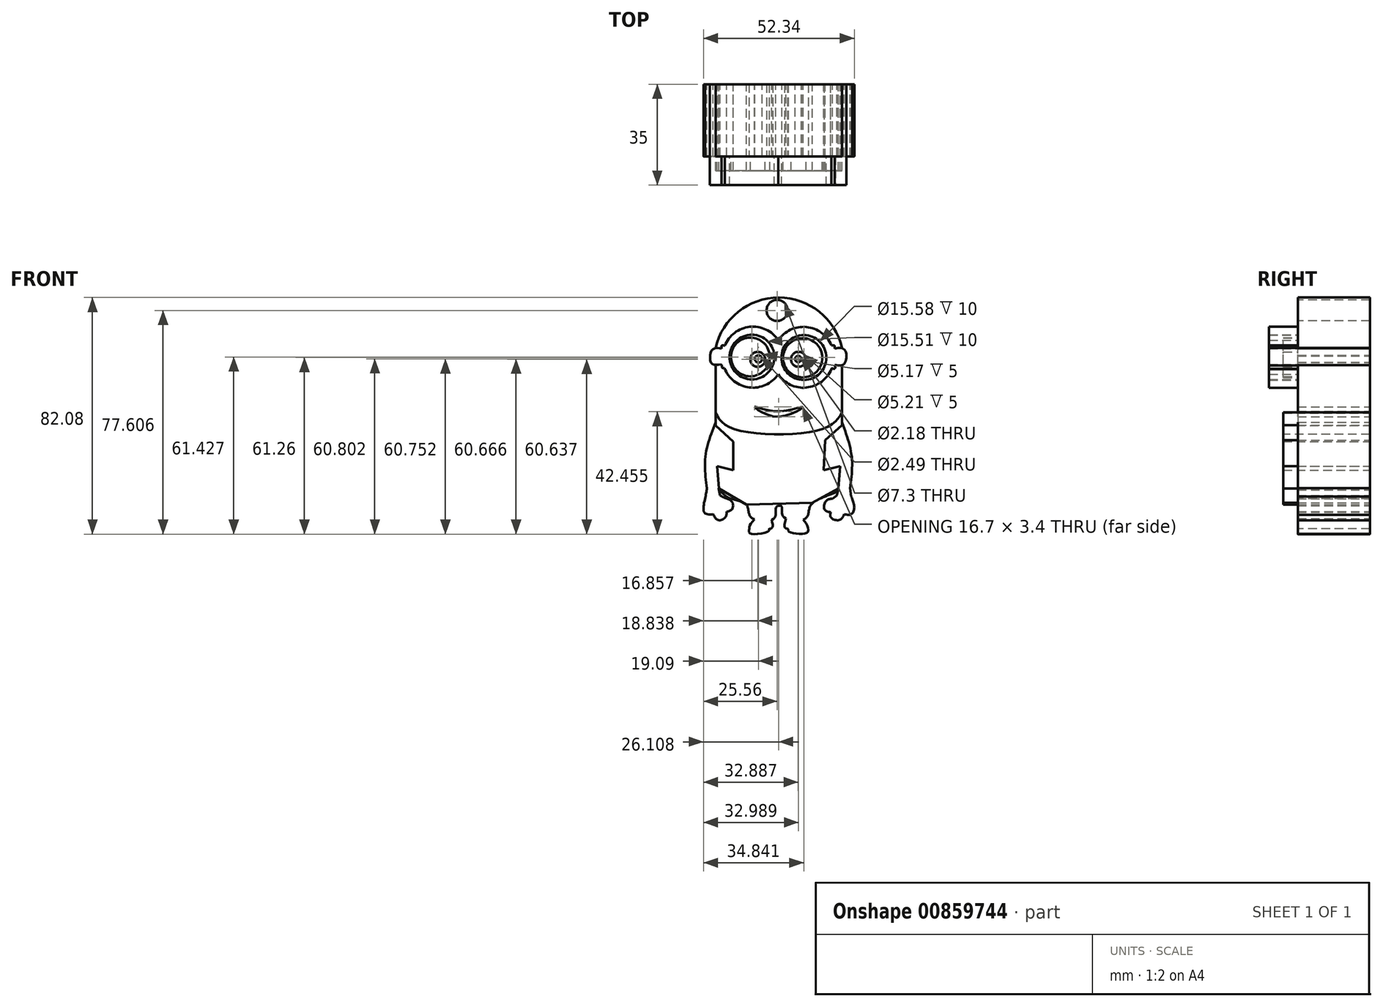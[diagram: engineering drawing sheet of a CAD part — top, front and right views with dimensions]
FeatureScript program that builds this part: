
annotation { "Feature Type Name" : "Feature", "Feature Type Description" : "" }
export const myFeature = defineFeature(function(context is Context, id is Id, definition is map)
    precondition{}
    {
        {
            var Q0;
            Q0=qCreatedBy(makeId("Front.planeOp"),FACE);
            var sketch = newSketch(context, id + "F0", { "sketchPlane" : qUnion([Q0])});
            skCircle(sketch, "E0", {"center": v(9.28, 20.5) * mm, "radius": 7.79 * mm});
            skPoint(sketch, "E0.first.point", {"position": v(9.52, 28.28) * mm});
            skPoint(sketch, "E0.second.point", {"position": v(17.06, 20.1) * mm});
            skPoint(sketch, "E0.third.point", {"position": v(3.92, 14.85) * mm});
            skCircle(sketch, "E1", {"center": v(-8.7, 20.67) * mm, "radius": 7.75 * mm});
            skPoint(sketch, "E1.first.point", {"position": v(-9.22, 28.4) * mm});
            skPoint(sketch, "E1.second.point", {"position": v(-0.97, 20.1) * mm});
            skPoint(sketch, "E1.third.point", {"position": v(-16.11, 18.39) * mm});
            skArc(sketch, "E2", {"start": v(0.4, 26.53) * mm, "mid": v(-18.96, 20.65) * mm, "end": v(0.38, 14.7) * mm});
            skPoint(sketch, "E2.first.point", {"position": v(-8.74, 31.2) * mm});
            skPoint(sketch, "E2.second.point", {"position": v(-8.44, 10.05) * mm});
            skPoint(sketch, "E2.third.point", {"position": v(-18.93, 19.83) * mm});
            skArc(sketch, "E3", {"start": v(0.38, 14.7) * mm, "mid": v(19.7, 20.59) * mm, "end": v(0.4, 26.53) * mm});
            skPoint(sketch, "E3.first.point", {"position": v(9.59, 31.15) * mm});
            skPoint(sketch, "E3.second.point", {"position": v(19.66, 19.83) * mm});
            skPoint(sketch, "E3.third.point", {"position": v(8, 10.11) * mm});
            skFitSpline(sketch, "E4", {"points": [v(18.85, 24.73) * mm, v(19.87, 24.63) * mm, v(19.97, 23.65) * mm], "startDerivative": vector(2.5, 0.28) * mm, "endDerivative": vector(-0.27, -2.43) * mm});
            skFitSpline(sketch, "E5", {"points": [v(19.97, 23.65) * mm, v(23.52, 23.1) * mm, v(23.29, 18.32) * mm, v(20.01, 18) * mm], "startDerivative": vector(13.3, 1.85) * mm, "endDerivative": vector(-12.33, 2.55) * mm});
            skFitSpline(sketch, "E6", {"points": [v(20.01, 18) * mm, v(20.01, 16.69) * mm, v(18.94, 16.7) * mm, v(18.85, 16.48) * mm], "startDerivative": vector(1, -4.05) * mm, "endDerivative": vector(-0.02, -1.55) * mm});
            skFitSpline(sketch, "E7", {"points": [v(-18.17, 24.63) * mm, v(-19.18, 24.63) * mm, v(-19.25, 23.65) * mm], "startDerivative": vector(-2.46, 0.5) * mm, "endDerivative": vector(0.31, -2.46) * mm});
            skFitSpline(sketch, "E8", {"points": [v(-19.25, 23.65) * mm, v(-22.57, 23.1) * mm, v(-22.44, 18.29) * mm, v(-19.25, 18) * mm, v(-19.07, 17.04) * mm, v(-18.29, 16.92) * mm], "startDerivative": vector(-16.18, 2.6) * mm, "endDerivative": vector(8.86, 1.17) * mm});
            skCircle(sketch, "E9", {"center": v(-9.3, 20.73) * mm, "radius": 6.74 * mm});
            skPoint(sketch, "E9.first.point", {"position": v(-8.05, 27.35) * mm});
            skPoint(sketch, "E9.second.point", {"position": v(-9.11, 14) * mm});
            skPoint(sketch, "E9.third.point", {"position": v(-10.63, 14.13) * mm});
            skCircle(sketch, "E10", {"center": v(-6.72, 19.88) * mm, "radius": 2.58 * mm});
            skPoint(sketch, "E10.first.point", {"position": v(-6.73, 22.46) * mm});
            skPoint(sketch, "E10.second.point", {"position": v(-6.53, 17.3) * mm});
            skPoint(sketch, "E10.third.point", {"position": v(-8.98, 18.62) * mm});
            skCircle(sketch, "E11", {"center": v(-6.47, 20.04) * mm, "radius": 1.25 * mm});
            skPoint(sketch, "E11.first.point", {"position": v(-7.06, 21.14) * mm});
            skPoint(sketch, "E11.second.point", {"position": v(-6.72, 18.82) * mm});
            skPoint(sketch, "E11.third.point", {"position": v(-7.46, 19.29) * mm});
            skCircle(sketch, "E12", {"center": v(7.33, 20) * mm, "radius": 1.1 * mm});
            skPoint(sketch, "E12.first.point", {"position": v(7.16, 21.07) * mm});
            skPoint(sketch, "E12.second.point", {"position": v(8.41, 19.88) * mm});
            skPoint(sketch, "E12.third.point", {"position": v(6.5, 19.29) * mm});
            skCircle(sketch, "E13", {"center": v(7.43, 19.9) * mm, "radius": 2.6 * mm});
            skPoint(sketch, "E13.first.point", {"position": v(8.55, 22.26) * mm});
            skPoint(sketch, "E13.second.point", {"position": v(7.33, 17.3) * mm});
            skPoint(sketch, "E13.third.point", {"position": v(5.24, 18.5) * mm});
            skCircle(sketch, "E14", {"center": v(8.89, 20.42) * mm, "radius": 6.8 * mm});
            skPoint(sketch, "E14.first.point", {"position": v(10.53, 27.02) * mm});
            skPoint(sketch, "E14.second.point", {"position": v(11.46, 14.13) * mm});
            skPoint(sketch, "E14.third.point", {"position": v(3.92, 15.78) * mm});
            skSolve(sketch);
        }
        {
            var Q0;
            Q0=qCreatedBy(makeId("Front.planeOp"),FACE);
            var sketch = newSketch(context, id + "F1", { "sketchPlane" : qUnion([Q0])});
            skArc(sketch, "E15", {"start": v(22.5, 23.85) * mm, "mid": v(0.59, 41.32) * mm, "end": v(-21.33, 23.85) * mm});
            skPoint(sketch, "E15.first.point", {"position": v(0, 41.3) * mm});
            skPoint(sketch, "E15.second.point", {"position": v(22.5, 23.85) * mm});
            skPoint(sketch, "E15.third.point", {"position": v(-21.33, 23.85) * mm});
            skLineSegment(sketch, "E16.left", {"start": v(22.5, 23.85) * mm, "end": v(22.5, -1.97) * mm});
            skLineSegment(sketch, "E16.right", {"start": v(-21.33, 23.85) * mm, "end": v(-21.33, -1.97) * mm});
            skFitSpline(sketch, "E17", {"points": [v(-21.33, -1.97) * mm, v(-24.85, -13.62) * mm, v(-24.35, -24.85) * mm], "startDerivative": vector(-8.93, -22.82) * mm, "endDerivative": vector(2.96, -22.94) * mm});
            skFitSpline(sketch, "E18", {"points": [v(-19.42, -9.62) * mm, v(-21.04, -17.3) * mm, v(-20.3, -24.79) * mm], "startDerivative": vector(-4.4, -15.21) * mm, "endDerivative": vector(2.68, -15.12) * mm});
            skFitSpline(sketch, "E19", {"points": [v(22.5, -1.97) * mm, v(25.85, -13.64) * mm, v(25.32, -24.79) * mm], "startDerivative": vector(8.52, -22.88) * mm, "endDerivative": vector(-2.95, -22.75) * mm});
            skFitSpline(sketch, "E20", {"points": [v(20.43, -9.8) * mm, v(21.95, -15.7) * mm, v(21.35, -24.79) * mm], "startDerivative": vector(4.39, -12.32) * mm, "endDerivative": vector(-2.31, -17.47) * mm});
            skFitSpline(sketch, "E21", {"points": [v(-24.35, -24.85) * mm, v(-24.89, -27.96) * mm, v(-25.28, -33.24) * mm, v(-22.16, -33.85) * mm], "startDerivative": vector(-1.2, -8.73) * mm, "endDerivative": vector(12.85, 0.91) * mm});
            skFitSpline(sketch, "E22", {"points": [v(-22.16, -33.85) * mm, v(-20.3, -35.9) * mm, v(-17.88, -34.8) * mm, v(-17.55, -32.96) * mm], "startDerivative": vector(4.35, -7.95) * mm, "endDerivative": vector(-0.37, 6.48) * mm});
            skFitSpline(sketch, "E23", {"points": [v(-17.55, -32.96) * mm, v(-15.71, -32.18) * mm, v(-15.32, -30.24) * mm, v(-16.32, -28.85) * mm, v(-17.55, -28.4) * mm, v(-19.77, -27.29) * mm], "startDerivative": vector(10.29, 2.19) * mm, "endDerivative": vector(-10.31, 5.77) * mm});
            skFitSpline(sketch, "E24", {"points": [v(-19.77, -27.29) * mm, v(-20.3, -24.79) * mm], "startDerivative": vector(-0.52, 2.5) * mm, "endDerivative": vector(-0.52, 2.5) * mm});
            skFitSpline(sketch, "E25", {"points": [v(25.32, -24.79) * mm, v(25.72, -27.73) * mm], "startDerivative": vector(0.4, -2.94) * mm, "endDerivative": vector(0.4, -2.94) * mm});
            skFitSpline(sketch, "E26", {"points": [v(25.72, -27.73) * mm, v(26.66, -30.4) * mm, v(26.55, -32.74) * mm, v(25.32, -33.96) * mm, v(23.33, -33.8) * mm], "startDerivative": vector(4.04, -9.36) * mm, "endDerivative": vector(-8.88, 2.18) * mm});
            skFitSpline(sketch, "E27", {"points": [v(23.33, -33.8) * mm, v(22.1, -35.57) * mm, v(19.99, -35.8) * mm, v(18.49, -34.57) * mm, v(18.6, -33.13) * mm], "startDerivative": vector(-3.66, -7.88) * mm, "endDerivative": vector(1.93, 6.8) * mm});
            skFitSpline(sketch, "E28", {"points": [v(18.6, -33.13) * mm, v(16.65, -32.4) * mm, v(16.37, -30.4) * mm, v(17.65, -28.73) * mm, v(19.21, -28.51) * mm], "startDerivative": vector(-8.86, 1.43) * mm, "endDerivative": vector(7.12, -0.19) * mm});
            skFitSpline(sketch, "E29", {"points": [v(19.21, -28.51) * mm, v(20.71, -27.29) * mm], "startDerivative": vector(1.5, 1.22) * mm, "endDerivative": vector(1.5, 1.22) * mm});
            skFitSpline(sketch, "E30", {"points": [v(20.71, -27.29) * mm, v(21.35, -24.79) * mm], "startDerivative": vector(0.64, 2.5) * mm, "endDerivative": vector(0.64, 2.5) * mm});
            skFitSpline(sketch, "E31", {"points": [v(-20.3, -24.79) * mm, v(-16.53, -28.27) * mm, v(-10.59, -30.63) * mm, v(-8.93, -35) * mm, v(-0.9, -35.12) * mm, v(-0.32, -31.43) * mm, v(1.52, -31.1) * mm, v(2.18, -34.7) * mm, v(9.99, -35.22) * mm, v(11.81, -30.54) * mm, v(20.71, -25.96) * mm, v(21.35, -24.79) * mm], "startDerivative": vector(32.18, -43.66) * mm, "endDerivative": vector(2.2, 24.18) * mm});
            skFitSpline(sketch, "E32", {"points": [v(-1.9, -35.78) * mm, v(-1.55, -37.96) * mm, v(-2.14, -38.83) * mm, v(-2.76, -38.88) * mm, v(-2.84, -39.52) * mm, v(-7.07, -40.74) * mm, v(-9.67, -40.24) * mm, v(-9.67, -39.15) * mm, v(-9.55, -37.96) * mm, v(-7.9, -35.62) * mm], "startDerivative": vector(5.3, -18.32) * mm, "endDerivative": vector(14.78, 17.3) * mm});
            skFitSpline(sketch, "E33", {"points": [v(9.07, -35.7) * mm, v(10.5, -37.81) * mm, v(10.76, -39.87) * mm, v(9.2, -40.64) * mm, v(5.31, -40.34) * mm, v(3.83, -39.55) * mm, v(3.78, -38.93) * mm, v(3.16, -38.78) * mm, v(2.56, -38.23) * mm, v(3.05, -35.39) * mm], "startDerivative": vector(11.76, -14.6) * mm, "endDerivative": vector(6.8, 23.47) * mm});
            skFitSpline(sketch, "E34", {"points": [v(-7.8, 3.4) * mm, v(0, 1.83) * mm, v(8.9, 3.32) * mm, v(0, 0) * mm, v(-7.8, 3.4) * mm]});
            skLineSegment(sketch, "E35", {"start": v(25.32, -24.79) * mm, "end": v(21.35, -24.79) * mm});
            skLineSegment(sketch, "E36", {"start": v(-20.3, -24.79) * mm, "end": v(-24.35, -24.85) * mm});
            skSolve(sketch);
        }
        {
            var Q0;
            Q0=qCreatedBy(makeId("Front.planeOp"),FACE);
            var sketch = newSketch(context, id + "F2", { "sketchPlane" : qUnion([Q0])});
            skFitSpline(sketch, "E37", {"points": [v(-21.36, 1.21) * mm, v(-15.26, -4.16) * mm, v(16.06, -4.18) * mm, v(22.5, 1.46) * mm], "startDerivative": vector(14.47, -24.14) * mm, "endDerivative": vector(15.11, 24.76) * mm});
            skFitSpline(sketch, "E38", {"points": [v(22.5, 1.46) * mm, v(22.5, -2.9) * mm], "startDerivative": vector(0, -4.36) * mm, "endDerivative": vector(0, -4.36) * mm});
            skFitSpline(sketch, "E39", {"points": [v(22.5, -2.9) * mm, v(16.6, -8.2) * mm], "startDerivative": vector(-5.9, -5.3) * mm, "endDerivative": vector(-5.9, -5.3) * mm});
            skFitSpline(sketch, "E40", {"points": [v(16.6, -8.2) * mm, v(16.11, -18.6) * mm], "startDerivative": vector(-0.5, -10.4) * mm, "endDerivative": vector(-0.5, -10.4) * mm});
            skFitSpline(sketch, "E41", {"points": [v(16.11, -18.6) * mm, v(21.86, -17.18) * mm], "startDerivative": vector(5.75, 1.42) * mm, "endDerivative": vector(5.75, 1.42) * mm});
            skFitSpline(sketch, "E42", {"points": [v(21.86, -17.18) * mm, v(21.2, -24.9) * mm], "startDerivative": vector(-0.65, -7.72) * mm, "endDerivative": vector(-0.65, -7.72) * mm});
            skFitSpline(sketch, "E43", {"points": [v(21.2, -24.9) * mm, v(12.17, -29.91) * mm], "startDerivative": vector(-9.03, -5.01) * mm, "endDerivative": vector(-9.03, -5.01) * mm});
            skFitSpline(sketch, "E44", {"points": [v(12.17, -29.91) * mm, v(-10.66, -30.54) * mm], "startDerivative": vector(-22.83, -0.63) * mm, "endDerivative": vector(-22.83, -0.63) * mm});
            skFitSpline(sketch, "E45", {"points": [v(-10.66, -30.54) * mm, v(-20.1, -24.9) * mm], "startDerivative": vector(-9.45, 5.64) * mm, "endDerivative": vector(-9.45, 5.64) * mm});
            skFitSpline(sketch, "E46", {"points": [v(-20.1, -24.9) * mm, v(-20.83, -17.18) * mm], "startDerivative": vector(-0.72, 7.72) * mm, "endDerivative": vector(-0.72, 7.72) * mm});
            skFitSpline(sketch, "E47", {"points": [v(-20.83, -17.18) * mm, v(-15.27, -18.6) * mm], "startDerivative": vector(5.56, -1.42) * mm, "endDerivative": vector(5.56, -1.42) * mm});
            skFitSpline(sketch, "E48", {"points": [v(-15.27, -18.6) * mm, v(-15.27, -8.65) * mm], "startDerivative": vector(0, 9.95) * mm, "endDerivative": vector(0, 9.95) * mm});
            skFitSpline(sketch, "E49", {"points": [v(-15.27, -8.65) * mm, v(-21.28, -3.05) * mm], "startDerivative": vector(-6, 5.6) * mm, "endDerivative": vector(-6, 5.6) * mm});
            skFitSpline(sketch, "E50", {"points": [v(-21.28, -3.05) * mm, v(-21.36, 1.21) * mm], "startDerivative": vector(-0.08, 4.26) * mm, "endDerivative": vector(-0.08, 4.26) * mm});
            skSolve(sketch);
        }
        {
            var Q0;
            Q0 = qSketchRegion(id + "F1", true);
            extrude(context, id + "F3", {"entities" : qUnion([Q0]), "depth" : 25 * mm, "offsetDistance" : 25 * mm});
        }
        {
            var Q0;
            Q0=makeQuery(id+"F0.imprint","IMPRINT",FACE,{"disambiguationData":[TD([[makeQuery(id+"F0.imprint","IMPRINT",EDGE,{"derivedFrom":sQuery(id+"F0.wireOp",EDGE,"E0")}),-1.0]])]});
            var Q1;
            {var subQ0=sQuery(id+"F0.wireOp",EDGE,"E4");Q1=makeQuery(id+"F0.imprint","IMPRINT",FACE,{"disambiguationData":[TD([[makeQuery(id+"F0.imprint","IMPRINT",EDGE,{"derivedFrom":subQ0}),-1.0]])]});}
            var Q2;
            {var subQ0=sQuery(id+"F0.wireOp",EDGE,"E7");Q2=makeQuery(id+"F0.imprint","IMPRINT",FACE,{"disambiguationData":[TD([[makeQuery(id+"F0.imprint","IMPRINT",EDGE,{"derivedFrom":subQ0}),1.0]])]});}
            extrude(context, id + "F4", {"entities" : qUnion([Q0, Q1, Q2]), "operationType" : NewBodyOperationType.ADD, "depth" : 35 * mm, "offsetDistance" : 25 * mm});
        }
        {
            var Q0;
            Q0=makeQuery(id+"F0.imprint","IMPRINT",FACE,{"disambiguationData":[TD([[makeQuery(id+"F0.imprint","IMPRINT",EDGE,{"derivedFrom":sQuery(id+"F0.wireOp",EDGE,"E13")}),-1.0]])]});
            var Q1;
            Q1=makeQuery(id+"F0.imprint","IMPRINT",FACE,{"disambiguationData":[TD([[makeQuery(id+"F0.imprint","IMPRINT",EDGE,{"derivedFrom":sQuery(id+"F0.wireOp",EDGE,"E9")}),1.0]])]});
            extrude(context, id + "F5", {"entities" : qUnion([Q0, Q1]), "operationType" : NewBodyOperationType.ADD, "depth" : 30 * mm, "offsetDistance" : 25 * mm});
        }
        {
            var Q0;
            Q0=makeQuery(id+"F0.imprint","IMPRINT",FACE,{"disambiguationData":[TD([[makeQuery(id+"F0.imprint","IMPRINT",EDGE,{"derivedFrom":sQuery(id+"F0.wireOp",EDGE,"E12")}),1.0]])]});
            var Q1;
            Q1=makeQuery(id+"F0.imprint","IMPRINT",FACE,{"disambiguationData":[TD([[makeQuery(id+"F0.imprint","IMPRINT",EDGE,{"derivedFrom":sQuery(id+"F0.wireOp",EDGE,"E11")}),1.0]])]});
            extrude(context, id + "F6", {"entities" : qUnion([Q0, Q1]), "operationType" : NewBodyOperationType.REMOVE, "endBound" : BoundingType.THROUGH_ALL, "depth" : 42.6 * mm, "offsetDistance" : 25 * mm});
        }
        {
            var Q0;
            Q0=makeQuery(id+"F2.imprint","IMPRINT",FACE,{"disambiguationData":[TD([[makeQuery(id+"F2.imprint","IMPRINT",EDGE,{"derivedFrom":sQuery(id+"F2.wireOp",EDGE,"E37")}),-1.0]])]});
            extrude(context, id + "F7", {"entities" : qUnion([Q0]), "depth" : 30 * mm, "offsetDistance" : 25 * mm});
        }
        {
            var Q0;
            {var subQ0=sQuery(id+"F1.wireOp",EDGE,"E16.right");var subQ2=sQuery(id+"F1.wireOp",EDGE,"E16.left");var subQ6=sQuery(id+"F1.wireOp",EDGE,"E15");Q0=makeQuery(id+"F4.boolean.opBoolean","SPLIT",FACE,{"disambiguationData":[TD([makeQuery(id+"F3.opExtrude","SWEPT_FACE",FACE,{"disambiguationData":[OSD([subQ6])]})])],"derivedFrom":makeQuery(id+"F3.opExtrude","CAP_FACE",FACE,{"disambiguationData":[OSD([subQ6,subQ2,subQ0,sQuery(id+"F1.wireOp",EDGE,"E17"),sQuery(id+"F1.wireOp",EDGE,"E19"),sQuery(id+"F1.wireOp",EDGE,"E21"),sQuery(id+"F1.wireOp",EDGE,"E22"),sQuery(id+"F1.wireOp",EDGE,"E23"),sQuery(id+"F1.wireOp",EDGE,"E24"),sQuery(id+"F1.wireOp",EDGE,"E25"),sQuery(id+"F1.wireOp",EDGE,"E26"),sQuery(id+"F1.wireOp",EDGE,"E27"),sQuery(id+"F1.wireOp",EDGE,"E28"),sQuery(id+"F1.wireOp",EDGE,"E29"),sQuery(id+"F1.wireOp",EDGE,"E30"),sQuery(id+"F1.wireOp",EDGE,"E31"),sQuery(id+"F1.wireOp",EDGE,"E32"),sQuery(id+"F1.wireOp",EDGE,"E33"),sQuery(id+"F1.wireOp",EDGE,"E34")])],"isStart":false})});}
            var sketch = newSketch(context, id + "F8", { "sketchPlane" : qUnion([Q0])});
            skCircle(sketch, "E51", {"center": v(0, 36.85) * mm, "radius": 3.65 * mm});
            skSolve(sketch);
        }
        {
            var Q0;
            Q0=makeQuery(id+"F8.imprint","IMPRINT",FACE,{"disambiguationData":[TD([[makeQuery(id+"F8.imprint","IMPRINT",EDGE,{"derivedFrom":sQuery(id+"F8.wireOp",EDGE,"E51")}),1.0]])]});
            extrude(context, id + "F9", {"entities" : qUnion([Q0]), "operationType" : NewBodyOperationType.REMOVE, "endBound" : BoundingType.THROUGH_ALL, "oppositeDirection" : true, "depth" : 25 * mm, "offsetDistance" : 25 * mm});
        }
    });
